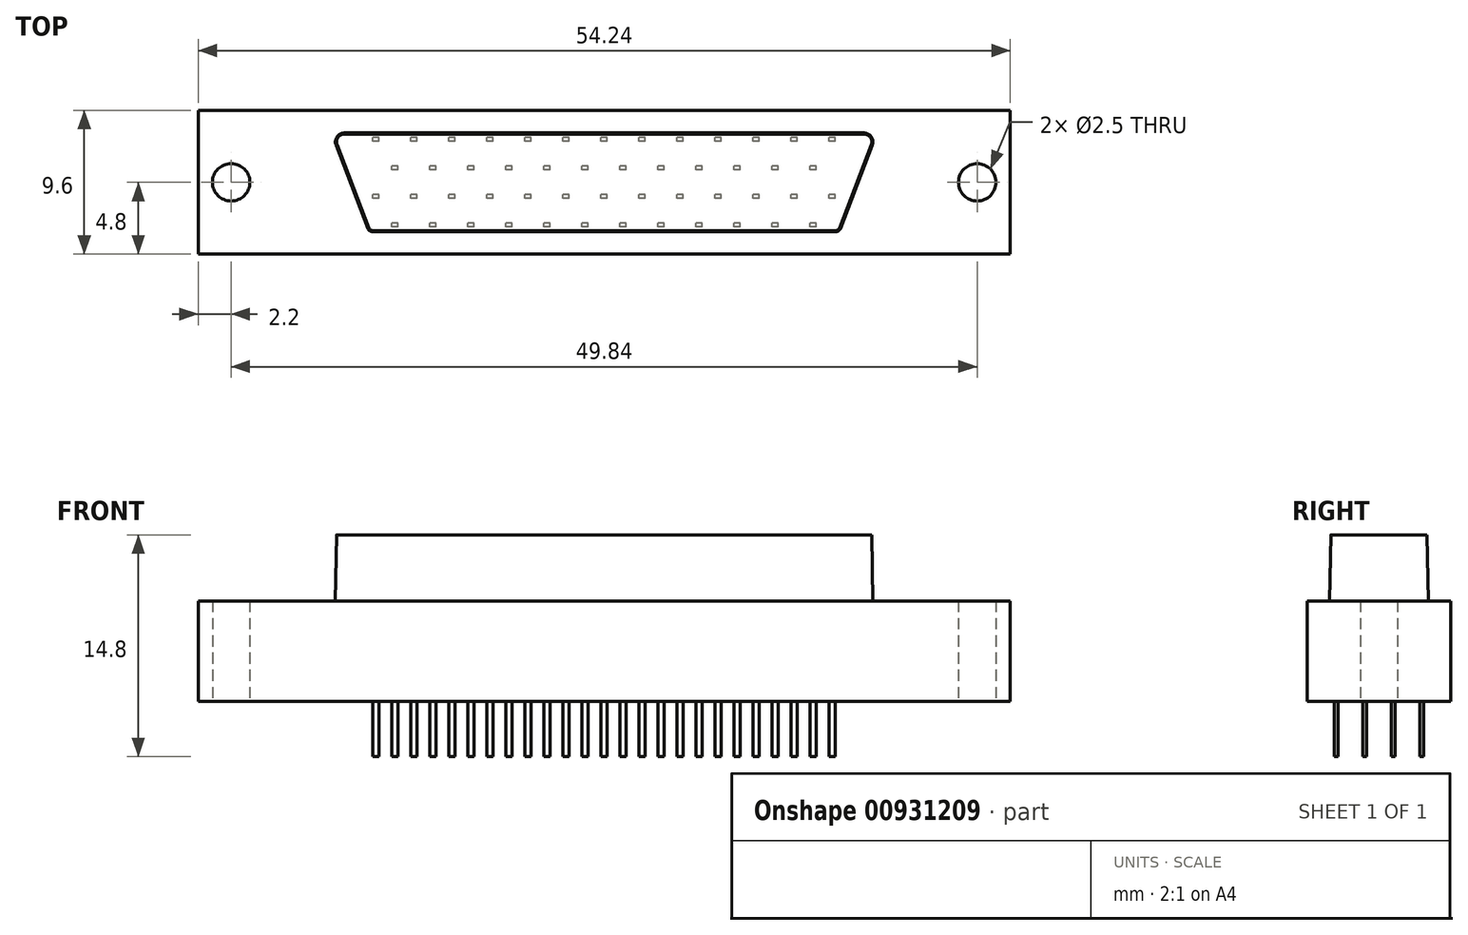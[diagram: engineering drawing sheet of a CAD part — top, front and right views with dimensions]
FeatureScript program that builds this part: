
annotation { "Feature Type Name" : "Feature", "Feature Type Description" : "" }
export const myFeature = defineFeature(function(context is Context, id is Id, definition is map)
    precondition{}
    {
        {
            var Q0;
            Q0=qCreatedBy(makeId("Top.planeOp"),FACE);
            var sketch = newSketch(context, id + "F0", { "sketchPlane" : qUnion([Q0])});
            skLineSegment(sketch, "E0.bottom", {"start": v(27.12, -4.8) * mm, "end": v(-27.12, -4.8) * mm});
            skLineSegment(sketch, "E0.top", {"start": v(27.12, 4.8) * mm, "end": v(-27.12, 4.8) * mm});
            skLineSegment(sketch, "E0.left", {"start": v(27.12, -4.8) * mm, "end": v(27.12, 4.8) * mm});
            skLineSegment(sketch, "E0.right", {"start": v(-27.12, -4.8) * mm, "end": v(-27.12, 4.8) * mm});
            skPoint(sketch, "E0.middle", {"position": v(0, 0) * mm});
            skCircle(sketch, "E1", {"center": v(24.92, 0) * mm, "radius": 1.25 * mm});
            skCircle(sketch, "E2.MirrorC", {"center": v(-24.92, 0) * mm, "radius": 1.25 * mm});
            skSolve(sketch);
        }
        {
            var Q0;
            Q0 = qSketchRegion(id + "F0", true);
            extrude(context, id + "F1", {"entities" : qUnion([Q0]), "depth" : 6.7 * mm, "offsetDistance" : 25 * mm, "symmetric" : true});
        }
        {
            var Q0;
            Q0=makeQuery(id+"F1.opExtrude","CAP_FACE",FACE,{"disambiguationData":[OSD([sQuery(id+"F0.wireOp",EDGE,"E0.bottom"),sQuery(id+"F0.wireOp",EDGE,"E0.top"),sQuery(id+"F0.wireOp",EDGE,"E0.left"),sQuery(id+"F0.wireOp",EDGE,"E0.right")])],"isStart":false});
            var sketch = newSketch(context, id + "F2", { "sketchPlane" : qUnion([Q0])});
            skLineSegment(sketch, "E3", {"start": v(-17.36, 3.3) * mm, "end": v(17.35, 3.3) * mm});
            skLineSegment(sketch, "E4", {"start": v(17.92, 2.48) * mm, "end": v(15.78, -3.1) * mm});
            skLineSegment(sketch, "E5", {"start": v(15.5, -3.3) * mm, "end": v(-15.5, -3.3) * mm});
            skLineSegment(sketch, "E6", {"start": v(-15.78, -3.1) * mm, "end": v(-17.92, 2.48) * mm});
            skPoint(sketch, "E7.visualSharp", {"position": v(-18.23, 3.3) * mm});
            skArc(sketch, "E7.filletArc", {"start": v(-17.36, 3.3) * mm, "mid": v(-17.85, 3.03) * mm, "end": v(-17.92, 2.48) * mm});
            skPoint(sketch, "E8.visualSharp", {"position": v(-15.7, -3.3) * mm});
            skArc(sketch, "E8.filletArc", {"start": v(-15.78, -3.1) * mm, "mid": v(-15.67, -3.24) * mm, "end": v(-15.5, -3.3) * mm});
            skPoint(sketch, "E9.visualSharp", {"position": v(18.23, 3.3) * mm});
            skArc(sketch, "E9.filletArc", {"start": v(17.92, 2.48) * mm, "mid": v(17.85, 3.03) * mm, "end": v(17.35, 3.3) * mm});
            skPoint(sketch, "E10.visualSharp", {"position": v(15.7, -3.3) * mm});
            skArc(sketch, "E10.filletArc", {"start": v(15.5, -3.3) * mm, "mid": v(15.67, -3.24) * mm, "end": v(15.78, -3.1) * mm});
            skSolve(sketch);
        }
        {
            var Q0;
            Q0=makeQuery(id+"F2.imprint","IMPRINT",FACE,{"disambiguationData":[TD([[makeQuery(id+"F2.imprint","IMPRINT",EDGE,{"derivedFrom":sQuery(id+"F2.wireOp",EDGE,"E3")}),-1.0]])]});
            extrude(context, id + "F3", {"entities" : qUnion([Q0]), "operationType" : NewBodyOperationType.ADD, "depth" : 4.4 * mm, "offsetDistance" : 25 * mm, "hasDraft" : true, "draftAngle" : 1 * degree, "draftPullDirection" : true});
        }
        {
            var Q0;
            Q0=makeQuery(id+"F1.opExtrude","CAP_FACE",FACE,{"disambiguationData":[OSD([sQuery(id+"F0.wireOp",EDGE,"E0.bottom"),sQuery(id+"F0.wireOp",EDGE,"E0.top"),sQuery(id+"F0.wireOp",EDGE,"E0.left"),sQuery(id+"F0.wireOp",EDGE,"E0.right"),sQuery(id+"F0.wireOp",EDGE,"E1"),sQuery(id+"F0.wireOp",EDGE,"E2.MirrorC")])],"isStart":true});
            var sketch = newSketch(context, id + "F4", { "sketchPlane" : qUnion([Q0])});
            skLineSegment(sketch, "E11.bottom", {"start": v(-15.03, -2.73) * mm, "end": v(-15.45, -2.73) * mm});
            skLineSegment(sketch, "E11.top", {"start": v(-15.03, -2.98) * mm, "end": v(-15.45, -2.98) * mm});
            skLineSegment(sketch, "E11.left", {"start": v(-15.03, -2.73) * mm, "end": v(-15.03, -2.98) * mm});
            skLineSegment(sketch, "E11.right", {"start": v(-15.45, -2.73) * mm, "end": v(-15.45, -2.98) * mm});
            skPoint(sketch, "E11.middle", {"position": v(-15.24, -2.86) * mm});
            skLineSegment(sketch, "E12.1.0.0", {"start": v(-12.49, -2.98) * mm, "end": v(-12.9, -2.98) * mm});
            skLineSegment(sketch, "E12.1.0.1", {"start": v(-12.9, -2.73) * mm, "end": v(-12.9, -2.98) * mm});
            skLineSegment(sketch, "E12.1.0.2", {"start": v(-12.49, -2.73) * mm, "end": v(-12.9, -2.73) * mm});
            skLineSegment(sketch, "E12.1.0.3", {"start": v(-12.49, -2.73) * mm, "end": v(-12.49, -2.98) * mm});
            skPoint(sketch, "E12.1.0.4", {"position": v(-12.7, -2.86) * mm});
            skLineSegment(sketch, "E12.2.0.0", {"start": v(-9.95, -2.98) * mm, "end": v(-10.37, -2.98) * mm});
            skLineSegment(sketch, "E12.2.0.1", {"start": v(-10.37, -2.73) * mm, "end": v(-10.37, -2.98) * mm});
            skLineSegment(sketch, "E12.2.0.2", {"start": v(-9.95, -2.73) * mm, "end": v(-10.37, -2.73) * mm});
            skLineSegment(sketch, "E12.2.0.3", {"start": v(-9.95, -2.73) * mm, "end": v(-9.95, -2.98) * mm});
            skPoint(sketch, "E12.2.0.4", {"position": v(-10.16, -2.86) * mm});
            skLineSegment(sketch, "E12.3.0.0", {"start": v(-7.4, -2.98) * mm, "end": v(-7.83, -2.98) * mm});
            skLineSegment(sketch, "E12.3.0.1", {"start": v(-7.83, -2.73) * mm, "end": v(-7.83, -2.98) * mm});
            skLineSegment(sketch, "E12.3.0.2", {"start": v(-7.4, -2.73) * mm, "end": v(-7.83, -2.73) * mm});
            skLineSegment(sketch, "E12.3.0.3", {"start": v(-7.4, -2.73) * mm, "end": v(-7.4, -2.98) * mm});
            skPoint(sketch, "E12.3.0.4", {"position": v(-7.62, -2.86) * mm});
            skLineSegment(sketch, "E12.4.0.0", {"start": v(-4.87, -2.98) * mm, "end": v(-5.29, -2.98) * mm});
            skLineSegment(sketch, "E12.4.0.1", {"start": v(-5.29, -2.73) * mm, "end": v(-5.29, -2.98) * mm});
            skLineSegment(sketch, "E12.4.0.2", {"start": v(-4.87, -2.73) * mm, "end": v(-5.29, -2.73) * mm});
            skLineSegment(sketch, "E12.4.0.3", {"start": v(-4.87, -2.73) * mm, "end": v(-4.87, -2.98) * mm});
            skPoint(sketch, "E12.4.0.4", {"position": v(-5.08, -2.86) * mm});
            skLineSegment(sketch, "E12.5.0.0", {"start": v(-2.33, -2.98) * mm, "end": v(-2.75, -2.98) * mm});
            skLineSegment(sketch, "E12.5.0.1", {"start": v(-2.75, -2.73) * mm, "end": v(-2.75, -2.98) * mm});
            skLineSegment(sketch, "E12.5.0.2", {"start": v(-2.33, -2.73) * mm, "end": v(-2.75, -2.73) * mm});
            skLineSegment(sketch, "E12.5.0.3", {"start": v(-2.33, -2.73) * mm, "end": v(-2.33, -2.98) * mm});
            skPoint(sketch, "E12.5.0.4", {"position": v(-2.54, -2.86) * mm});
            skLineSegment(sketch, "E12.6.0.0", {"start": v(0.2, -2.98) * mm, "end": v(-0.2, -2.98) * mm});
            skLineSegment(sketch, "E12.6.0.1", {"start": v(-0.2, -2.73) * mm, "end": v(-0.2, -2.98) * mm});
            skLineSegment(sketch, "E12.6.0.2", {"start": v(0.2, -2.73) * mm, "end": v(-0.2, -2.73) * mm});
            skLineSegment(sketch, "E12.6.0.3", {"start": v(0.2, -2.73) * mm, "end": v(0.2, -2.98) * mm});
            skPoint(sketch, "E12.6.0.4", {"position": v(0, -2.86) * mm});
            skLineSegment(sketch, "E12.7.0.0", {"start": v(2.75, -2.98) * mm, "end": v(2.33, -2.98) * mm});
            skLineSegment(sketch, "E12.7.0.1", {"start": v(2.33, -2.73) * mm, "end": v(2.33, -2.98) * mm});
            skLineSegment(sketch, "E12.7.0.2", {"start": v(2.75, -2.73) * mm, "end": v(2.33, -2.73) * mm});
            skLineSegment(sketch, "E12.7.0.3", {"start": v(2.75, -2.73) * mm, "end": v(2.75, -2.98) * mm});
            skPoint(sketch, "E12.7.0.4", {"position": v(2.54, -2.86) * mm});
            skLineSegment(sketch, "E12.8.0.0", {"start": v(5.29, -2.98) * mm, "end": v(4.87, -2.98) * mm});
            skLineSegment(sketch, "E12.8.0.1", {"start": v(4.87, -2.73) * mm, "end": v(4.87, -2.98) * mm});
            skLineSegment(sketch, "E12.8.0.2", {"start": v(5.29, -2.73) * mm, "end": v(4.87, -2.73) * mm});
            skLineSegment(sketch, "E12.8.0.3", {"start": v(5.29, -2.73) * mm, "end": v(5.29, -2.98) * mm});
            skPoint(sketch, "E12.8.0.4", {"position": v(5.08, -2.86) * mm});
            skLineSegment(sketch, "E12.9.0.0", {"start": v(7.83, -2.98) * mm, "end": v(7.4, -2.98) * mm});
            skLineSegment(sketch, "E12.9.0.1", {"start": v(7.4, -2.73) * mm, "end": v(7.4, -2.98) * mm});
            skLineSegment(sketch, "E12.9.0.2", {"start": v(7.83, -2.73) * mm, "end": v(7.4, -2.73) * mm});
            skLineSegment(sketch, "E12.9.0.3", {"start": v(7.83, -2.73) * mm, "end": v(7.83, -2.98) * mm});
            skPoint(sketch, "E12.9.0.4", {"position": v(7.62, -2.86) * mm});
            skLineSegment(sketch, "E12.10.0.0", {"start": v(10.37, -2.98) * mm, "end": v(9.95, -2.98) * mm});
            skLineSegment(sketch, "E12.10.0.1", {"start": v(9.95, -2.73) * mm, "end": v(9.95, -2.98) * mm});
            skLineSegment(sketch, "E12.10.0.2", {"start": v(10.37, -2.73) * mm, "end": v(9.95, -2.73) * mm});
            skLineSegment(sketch, "E12.10.0.3", {"start": v(10.37, -2.73) * mm, "end": v(10.37, -2.98) * mm});
            skPoint(sketch, "E12.10.0.4", {"position": v(10.16, -2.86) * mm});
            skLineSegment(sketch, "E12.11.0.0", {"start": v(12.9, -2.98) * mm, "end": v(12.5, -2.98) * mm});
            skLineSegment(sketch, "E12.11.0.1", {"start": v(12.49, -2.73) * mm, "end": v(12.49, -2.98) * mm});
            skLineSegment(sketch, "E12.11.0.2", {"start": v(12.9, -2.73) * mm, "end": v(12.5, -2.73) * mm});
            skLineSegment(sketch, "E12.11.0.3", {"start": v(12.9, -2.73) * mm, "end": v(12.9, -2.98) * mm});
            skPoint(sketch, "E12.11.0.4", {"position": v(12.7, -2.86) * mm});
            skLineSegment(sketch, "E12.12.0.0", {"start": v(15.45, -2.98) * mm, "end": v(15.03, -2.98) * mm});
            skLineSegment(sketch, "E12.12.0.1", {"start": v(15.03, -2.73) * mm, "end": v(15.03, -2.98) * mm});
            skLineSegment(sketch, "E12.12.0.2", {"start": v(15.45, -2.73) * mm, "end": v(15.03, -2.73) * mm});
            skLineSegment(sketch, "E12.12.0.3", {"start": v(15.45, -2.73) * mm, "end": v(15.45, -2.98) * mm});
            skPoint(sketch, "E12.12.0.4", {"position": v(15.24, -2.86) * mm});
            skLineSegment(sketch, "E12.direction1", {"start": v(-15.45, -2.98) * mm, "end": v(-12.9, -2.98) * mm, "construction": true});
            skLineSegment(sketch, "E13.bottom", {"start": v(-13.76, -0.83) * mm, "end": v(-14.18, -0.83) * mm});
            skLineSegment(sketch, "E13.top", {"start": v(-13.76, -1.08) * mm, "end": v(-14.18, -1.08) * mm});
            skLineSegment(sketch, "E13.left", {"start": v(-13.76, -0.83) * mm, "end": v(-13.76, -1.08) * mm});
            skLineSegment(sketch, "E13.right", {"start": v(-14.18, -0.83) * mm, "end": v(-14.18, -1.08) * mm});
            skPoint(sketch, "E13.middle", {"position": v(-13.97, -0.95) * mm});
            skLineSegment(sketch, "E14.direction1", {"start": v(-14.18, -1.08) * mm, "end": v(-11.64, -1.08) * mm, "construction": true});
            skLineSegment(sketch, "E15.1.0.0", {"start": v(-11.22, -0.83) * mm, "end": v(-11.22, -1.08) * mm});
            skLineSegment(sketch, "E15.1.0.1", {"start": v(-11.22, -1.08) * mm, "end": v(-11.64, -1.08) * mm});
            skLineSegment(sketch, "E15.1.0.2", {"start": v(-11.64, -0.83) * mm, "end": v(-11.64, -1.08) * mm});
            skLineSegment(sketch, "E15.1.0.3", {"start": v(-11.22, -0.83) * mm, "end": v(-11.64, -0.83) * mm});
            skPoint(sketch, "E15.1.0.4", {"position": v(-11.43, -0.95) * mm});
            skLineSegment(sketch, "E15.2.0.0", {"start": v(-8.68, -0.83) * mm, "end": v(-8.68, -1.08) * mm});
            skLineSegment(sketch, "E15.2.0.1", {"start": v(-8.68, -1.08) * mm, "end": v(-9.1, -1.08) * mm});
            skLineSegment(sketch, "E15.2.0.2", {"start": v(-9.1, -0.83) * mm, "end": v(-9.1, -1.08) * mm});
            skLineSegment(sketch, "E15.2.0.3", {"start": v(-8.68, -0.83) * mm, "end": v(-9.1, -0.83) * mm});
            skPoint(sketch, "E15.2.0.4", {"position": v(-8.89, -0.95) * mm});
            skLineSegment(sketch, "E15.3.0.0", {"start": v(-6.14, -0.83) * mm, "end": v(-6.14, -1.08) * mm});
            skLineSegment(sketch, "E15.3.0.1", {"start": v(-6.14, -1.08) * mm, "end": v(-6.56, -1.08) * mm});
            skLineSegment(sketch, "E15.3.0.2", {"start": v(-6.56, -0.83) * mm, "end": v(-6.56, -1.08) * mm});
            skLineSegment(sketch, "E15.3.0.3", {"start": v(-6.14, -0.83) * mm, "end": v(-6.56, -0.83) * mm});
            skPoint(sketch, "E15.3.0.4", {"position": v(-6.35, -0.95) * mm});
            skLineSegment(sketch, "E15.4.0.0", {"start": v(-3.6, -0.83) * mm, "end": v(-3.6, -1.08) * mm});
            skLineSegment(sketch, "E15.4.0.1", {"start": v(-3.6, -1.08) * mm, "end": v(-4.02, -1.08) * mm});
            skLineSegment(sketch, "E15.4.0.2", {"start": v(-4.02, -0.83) * mm, "end": v(-4.02, -1.08) * mm});
            skLineSegment(sketch, "E15.4.0.3", {"start": v(-3.6, -0.83) * mm, "end": v(-4.02, -0.83) * mm});
            skPoint(sketch, "E15.4.0.4", {"position": v(-3.8, -0.95) * mm});
            skLineSegment(sketch, "E15.5.0.0", {"start": v(-1.06, -0.83) * mm, "end": v(-1.06, -1.08) * mm});
            skLineSegment(sketch, "E15.5.0.1", {"start": v(-1.06, -1.08) * mm, "end": v(-1.48, -1.08) * mm});
            skLineSegment(sketch, "E15.5.0.2", {"start": v(-1.48, -0.83) * mm, "end": v(-1.48, -1.08) * mm});
            skLineSegment(sketch, "E15.5.0.3", {"start": v(-1.06, -0.83) * mm, "end": v(-1.48, -0.83) * mm});
            skPoint(sketch, "E15.5.0.4", {"position": v(-1.27, -0.95) * mm});
            skLineSegment(sketch, "E15.6.0.0", {"start": v(1.48, -0.83) * mm, "end": v(1.48, -1.08) * mm});
            skLineSegment(sketch, "E15.6.0.1", {"start": v(1.48, -1.08) * mm, "end": v(1.06, -1.08) * mm});
            skLineSegment(sketch, "E15.6.0.2", {"start": v(1.06, -0.83) * mm, "end": v(1.06, -1.08) * mm});
            skLineSegment(sketch, "E15.6.0.3", {"start": v(1.48, -0.83) * mm, "end": v(1.06, -0.83) * mm});
            skPoint(sketch, "E15.6.0.4", {"position": v(1.27, -0.95) * mm});
            skLineSegment(sketch, "E15.7.0.0", {"start": v(4.02, -0.83) * mm, "end": v(4.02, -1.08) * mm});
            skLineSegment(sketch, "E15.7.0.1", {"start": v(4.02, -1.08) * mm, "end": v(3.6, -1.08) * mm});
            skLineSegment(sketch, "E15.7.0.2", {"start": v(3.6, -0.83) * mm, "end": v(3.6, -1.08) * mm});
            skLineSegment(sketch, "E15.7.0.3", {"start": v(4.02, -0.83) * mm, "end": v(3.6, -0.83) * mm});
            skPoint(sketch, "E15.7.0.4", {"position": v(3.81, -0.95) * mm});
            skLineSegment(sketch, "E15.8.0.0", {"start": v(6.56, -0.83) * mm, "end": v(6.56, -1.08) * mm});
            skLineSegment(sketch, "E15.8.0.1", {"start": v(6.56, -1.08) * mm, "end": v(6.14, -1.08) * mm});
            skLineSegment(sketch, "E15.8.0.2", {"start": v(6.14, -0.83) * mm, "end": v(6.14, -1.08) * mm});
            skLineSegment(sketch, "E15.8.0.3", {"start": v(6.56, -0.83) * mm, "end": v(6.14, -0.83) * mm});
            skPoint(sketch, "E15.8.0.4", {"position": v(6.35, -0.95) * mm});
            skLineSegment(sketch, "E15.9.0.0", {"start": v(9.1, -0.83) * mm, "end": v(9.1, -1.08) * mm});
            skLineSegment(sketch, "E15.9.0.1", {"start": v(9.1, -1.08) * mm, "end": v(8.68, -1.08) * mm});
            skLineSegment(sketch, "E15.9.0.2", {"start": v(8.68, -0.83) * mm, "end": v(8.68, -1.08) * mm});
            skLineSegment(sketch, "E15.9.0.3", {"start": v(9.1, -0.83) * mm, "end": v(8.68, -0.83) * mm});
            skPoint(sketch, "E15.9.0.4", {"position": v(8.9, -0.95) * mm});
            skLineSegment(sketch, "E15.10.0.0", {"start": v(11.64, -0.83) * mm, "end": v(11.64, -1.08) * mm});
            skLineSegment(sketch, "E15.10.0.1", {"start": v(11.64, -1.08) * mm, "end": v(11.22, -1.08) * mm});
            skLineSegment(sketch, "E15.10.0.2", {"start": v(11.22, -0.83) * mm, "end": v(11.22, -1.08) * mm});
            skLineSegment(sketch, "E15.10.0.3", {"start": v(11.64, -0.83) * mm, "end": v(11.22, -0.83) * mm});
            skPoint(sketch, "E15.10.0.4", {"position": v(11.43, -0.95) * mm});
            skLineSegment(sketch, "E15.11.0.0", {"start": v(14.18, -0.83) * mm, "end": v(14.18, -1.08) * mm});
            skLineSegment(sketch, "E15.11.0.1", {"start": v(14.18, -1.08) * mm, "end": v(13.76, -1.08) * mm});
            skLineSegment(sketch, "E15.11.0.2", {"start": v(13.76, -0.83) * mm, "end": v(13.76, -1.08) * mm});
            skLineSegment(sketch, "E15.11.0.3", {"start": v(14.18, -0.83) * mm, "end": v(13.76, -0.83) * mm});
            skPoint(sketch, "E15.11.0.4", {"position": v(13.97, -0.95) * mm});
            skPoint(sketch, "E16.1.0.0", {"position": v(2.54, 0.95) * mm});
            skPoint(sketch, "E16.1.0.1", {"position": v(-10.16, 0.95) * mm});
            skPoint(sketch, "E16.1.0.2", {"position": v(-7.62, 0.95) * mm});
            skPoint(sketch, "E16.1.0.3", {"position": v(0, 0.95) * mm});
            skPoint(sketch, "E16.1.0.4", {"position": v(-5.08, 0.95) * mm});
            skPoint(sketch, "E16.1.0.5", {"position": v(10.16, 0.95) * mm});
            skPoint(sketch, "E16.1.0.6", {"position": v(11.43, 2.86) * mm});
            skPoint(sketch, "E16.1.0.7", {"position": v(15.24, 0.95) * mm});
            skPoint(sketch, "E16.1.0.8", {"position": v(3.81, 2.86) * mm});
            skPoint(sketch, "E16.1.0.9", {"position": v(6.35, 2.86) * mm});
            skPoint(sketch, "E16.1.0.10", {"position": v(-15.24, 0.95) * mm});
            skPoint(sketch, "E16.1.0.11", {"position": v(13.97, 2.86) * mm});
            skPoint(sketch, "E16.1.0.12", {"position": v(5.08, 0.95) * mm});
            skPoint(sketch, "E16.1.0.13", {"position": v(1.27, 2.86) * mm});
            skPoint(sketch, "E16.1.0.14", {"position": v(-3.8, 2.86) * mm});
            skPoint(sketch, "E16.1.0.15", {"position": v(-2.54, 0.95) * mm});
            skPoint(sketch, "E16.1.0.16", {"position": v(-1.27, 2.86) * mm});
            skPoint(sketch, "E16.1.0.17", {"position": v(12.7, 0.95) * mm});
            skPoint(sketch, "E16.1.0.18", {"position": v(-6.35, 2.86) * mm});
            skPoint(sketch, "E16.1.0.19", {"position": v(-13.97, 2.86) * mm});
            skPoint(sketch, "E16.1.0.20", {"position": v(8.9, 2.86) * mm});
            skPoint(sketch, "E16.1.0.21", {"position": v(-11.43, 2.86) * mm});
            skPoint(sketch, "E16.1.0.22", {"position": v(7.62, 0.95) * mm});
            skPoint(sketch, "E16.1.0.23", {"position": v(-8.89, 2.86) * mm});
            skLineSegment(sketch, "E16.1.0.24", {"start": v(-14.18, 2.73) * mm, "end": v(-11.64, 2.73) * mm, "construction": true});
            skPoint(sketch, "E16.1.0.25", {"position": v(-12.7, 0.95) * mm});
            skLineSegment(sketch, "E16.1.0.26", {"start": v(-15.45, 0.83) * mm, "end": v(-12.9, 0.83) * mm, "construction": true});
            skLineSegment(sketch, "E16.1.0.27", {"start": v(-14.18, 2.73) * mm, "end": v(-11.64, 2.73) * mm, "construction": true});
            skLineSegment(sketch, "E16.1.0.28", {"start": v(9.1, 2.73) * mm, "end": v(8.68, 2.73) * mm});
            skLineSegment(sketch, "E16.1.0.29", {"start": v(1.06, 2.98) * mm, "end": v(1.06, 2.73) * mm});
            skLineSegment(sketch, "E16.1.0.30", {"start": v(9.1, 2.98) * mm, "end": v(8.68, 2.98) * mm});
            skLineSegment(sketch, "E16.1.0.31", {"start": v(15.45, 1.08) * mm, "end": v(15.03, 1.08) * mm});
            skLineSegment(sketch, "E16.1.0.32", {"start": v(11.64, 2.98) * mm, "end": v(11.22, 2.98) * mm});
            skLineSegment(sketch, "E16.1.0.33", {"start": v(-3.6, 2.73) * mm, "end": v(-4.02, 2.73) * mm});
            skLineSegment(sketch, "E16.1.0.34", {"start": v(-2.33, 0.83) * mm, "end": v(-2.75, 0.83) * mm});
            skLineSegment(sketch, "E16.1.0.35", {"start": v(11.64, 2.73) * mm, "end": v(11.22, 2.73) * mm});
            skLineSegment(sketch, "E16.1.0.36", {"start": v(10.37, 1.08) * mm, "end": v(9.95, 1.08) * mm});
            skLineSegment(sketch, "E16.1.0.37", {"start": v(2.33, 1.08) * mm, "end": v(2.33, 0.83) * mm});
            skLineSegment(sketch, "E16.1.0.38", {"start": v(12.9, 1.08) * mm, "end": v(12.5, 1.08) * mm});
            skLineSegment(sketch, "E16.1.0.39", {"start": v(14.18, 2.98) * mm, "end": v(14.18, 2.73) * mm});
            skLineSegment(sketch, "E16.1.0.40", {"start": v(13.76, 2.98) * mm, "end": v(13.76, 2.73) * mm});
            skLineSegment(sketch, "E16.1.0.41", {"start": v(-2.33, 1.08) * mm, "end": v(-2.33, 0.83) * mm});
            skLineSegment(sketch, "E16.1.0.42", {"start": v(0.2, 0.83) * mm, "end": v(-0.2, 0.83) * mm});
            skLineSegment(sketch, "E16.1.0.43", {"start": v(10.37, 1.08) * mm, "end": v(10.37, 0.83) * mm});
            skLineSegment(sketch, "E16.1.0.44", {"start": v(2.75, 1.08) * mm, "end": v(2.75, 0.83) * mm});
            skLineSegment(sketch, "E16.1.0.45", {"start": v(-1.06, 2.73) * mm, "end": v(-1.48, 2.73) * mm});
            skLineSegment(sketch, "E16.1.0.46", {"start": v(7.4, 1.08) * mm, "end": v(7.4, 0.83) * mm});
            skLineSegment(sketch, "E16.1.0.47", {"start": v(-8.68, 2.98) * mm, "end": v(-8.68, 2.73) * mm});
            skLineSegment(sketch, "E16.1.0.48", {"start": v(-7.4, 1.08) * mm, "end": v(-7.83, 1.08) * mm});
            skLineSegment(sketch, "E16.1.0.49", {"start": v(1.48, 2.73) * mm, "end": v(1.06, 2.73) * mm});
            skLineSegment(sketch, "E16.1.0.50", {"start": v(0.2, 1.08) * mm, "end": v(-0.2, 1.08) * mm});
            skLineSegment(sketch, "E16.1.0.51", {"start": v(4.87, 1.08) * mm, "end": v(4.87, 0.83) * mm});
            skLineSegment(sketch, "E16.1.0.52", {"start": v(-4.87, 1.08) * mm, "end": v(-4.87, 0.83) * mm});
            skLineSegment(sketch, "E16.1.0.53", {"start": v(-8.68, 2.73) * mm, "end": v(-9.1, 2.73) * mm});
            skLineSegment(sketch, "E16.1.0.54", {"start": v(-7.4, 1.08) * mm, "end": v(-7.4, 0.83) * mm});
            skLineSegment(sketch, "E16.1.0.55", {"start": v(5.29, 1.08) * mm, "end": v(4.87, 1.08) * mm});
            skLineSegment(sketch, "E16.1.0.56", {"start": v(7.83, 0.83) * mm, "end": v(7.4, 0.83) * mm});
            skLineSegment(sketch, "E16.1.0.57", {"start": v(2.75, 1.08) * mm, "end": v(2.33, 1.08) * mm});
            skLineSegment(sketch, "E16.1.0.58", {"start": v(12.9, 1.08) * mm, "end": v(12.9, 0.83) * mm});
            skLineSegment(sketch, "E16.1.0.59", {"start": v(1.48, 2.98) * mm, "end": v(1.48, 2.73) * mm});
            skLineSegment(sketch, "E16.1.0.60", {"start": v(14.18, 2.98) * mm, "end": v(13.76, 2.98) * mm});
            skLineSegment(sketch, "E16.1.0.61", {"start": v(6.56, 2.73) * mm, "end": v(6.14, 2.73) * mm});
            skLineSegment(sketch, "E16.1.0.62", {"start": v(4.02, 2.98) * mm, "end": v(3.6, 2.98) * mm});
            skLineSegment(sketch, "E16.1.0.63", {"start": v(-6.14, 2.73) * mm, "end": v(-6.56, 2.73) * mm});
            skLineSegment(sketch, "E16.1.0.64", {"start": v(3.6, 2.98) * mm, "end": v(3.6, 2.73) * mm});
            skLineSegment(sketch, "E16.1.0.65", {"start": v(10.37, 0.83) * mm, "end": v(9.95, 0.83) * mm});
            skLineSegment(sketch, "E16.1.0.66", {"start": v(-2.75, 1.08) * mm, "end": v(-2.75, 0.83) * mm});
            skLineSegment(sketch, "E16.1.0.67", {"start": v(7.83, 1.08) * mm, "end": v(7.83, 0.83) * mm});
            skLineSegment(sketch, "E16.1.0.68", {"start": v(-7.83, 1.08) * mm, "end": v(-7.83, 0.83) * mm});
            skLineSegment(sketch, "E16.1.0.69", {"start": v(14.18, 2.73) * mm, "end": v(13.76, 2.73) * mm});
            skLineSegment(sketch, "E16.1.0.70", {"start": v(-1.48, 2.98) * mm, "end": v(-1.48, 2.73) * mm});
            skLineSegment(sketch, "E16.1.0.71", {"start": v(-6.14, 2.98) * mm, "end": v(-6.14, 2.73) * mm});
            skLineSegment(sketch, "E16.1.0.72", {"start": v(8.68, 2.98) * mm, "end": v(8.68, 2.73) * mm});
            skLineSegment(sketch, "E16.1.0.73", {"start": v(9.1, 2.98) * mm, "end": v(9.1, 2.73) * mm});
            skLineSegment(sketch, "E16.1.0.74", {"start": v(4.02, 2.73) * mm, "end": v(3.6, 2.73) * mm});
            skLineSegment(sketch, "E16.1.0.75", {"start": v(5.29, 1.08) * mm, "end": v(5.29, 0.83) * mm});
            skLineSegment(sketch, "E16.1.0.76", {"start": v(-5.29, 1.08) * mm, "end": v(-5.29, 0.83) * mm});
            skLineSegment(sketch, "E16.1.0.77", {"start": v(1.48, 2.98) * mm, "end": v(1.06, 2.98) * mm});
            skLineSegment(sketch, "E16.1.0.78", {"start": v(-4.87, 1.08) * mm, "end": v(-5.29, 1.08) * mm});
            skLineSegment(sketch, "E16.1.0.79", {"start": v(11.64, 2.98) * mm, "end": v(11.64, 2.73) * mm});
            skLineSegment(sketch, "E16.1.0.80", {"start": v(12.9, 0.83) * mm, "end": v(12.5, 0.83) * mm});
            skLineSegment(sketch, "E16.1.0.81", {"start": v(-4.02, 2.98) * mm, "end": v(-4.02, 2.73) * mm});
            skLineSegment(sketch, "E16.1.0.82", {"start": v(-8.68, 2.98) * mm, "end": v(-9.1, 2.98) * mm});
            skLineSegment(sketch, "E16.1.0.83", {"start": v(2.75, 0.83) * mm, "end": v(2.33, 0.83) * mm});
            skLineSegment(sketch, "E16.1.0.84", {"start": v(4.02, 2.98) * mm, "end": v(4.02, 2.73) * mm});
            skLineSegment(sketch, "E16.1.0.85", {"start": v(6.14, 2.98) * mm, "end": v(6.14, 2.73) * mm});
            skLineSegment(sketch, "E16.1.0.86", {"start": v(-3.6, 2.98) * mm, "end": v(-4.02, 2.98) * mm});
            skLineSegment(sketch, "E16.1.0.87", {"start": v(9.95, 1.08) * mm, "end": v(9.95, 0.83) * mm});
            skLineSegment(sketch, "E16.1.0.88", {"start": v(15.45, 1.08) * mm, "end": v(15.45, 0.83) * mm});
            skLineSegment(sketch, "E16.1.0.89", {"start": v(6.56, 2.98) * mm, "end": v(6.14, 2.98) * mm});
            skLineSegment(sketch, "E16.1.0.90", {"start": v(-0.2, 1.08) * mm, "end": v(-0.2, 0.83) * mm});
            skLineSegment(sketch, "E16.1.0.91", {"start": v(15.03, 1.08) * mm, "end": v(15.03, 0.83) * mm});
            skLineSegment(sketch, "E16.1.0.92", {"start": v(-1.06, 2.98) * mm, "end": v(-1.06, 2.73) * mm});
            skLineSegment(sketch, "E16.1.0.93", {"start": v(-1.06, 2.98) * mm, "end": v(-1.48, 2.98) * mm});
            skLineSegment(sketch, "E16.1.0.94", {"start": v(-6.14, 2.98) * mm, "end": v(-6.56, 2.98) * mm});
            skLineSegment(sketch, "E16.1.0.95", {"start": v(-4.87, 0.83) * mm, "end": v(-5.29, 0.83) * mm});
            skLineSegment(sketch, "E16.1.0.96", {"start": v(5.29, 0.83) * mm, "end": v(4.87, 0.83) * mm});
            skLineSegment(sketch, "E16.1.0.97", {"start": v(15.45, 0.83) * mm, "end": v(15.03, 0.83) * mm});
            skLineSegment(sketch, "E16.1.0.98", {"start": v(-9.1, 2.98) * mm, "end": v(-9.1, 2.73) * mm});
            skLineSegment(sketch, "E16.1.0.99", {"start": v(-3.6, 2.98) * mm, "end": v(-3.6, 2.73) * mm});
            skLineSegment(sketch, "E16.1.0.100", {"start": v(6.56, 2.98) * mm, "end": v(6.56, 2.73) * mm});
            skLineSegment(sketch, "E16.1.0.101", {"start": v(-2.33, 1.08) * mm, "end": v(-2.75, 1.08) * mm});
            skLineSegment(sketch, "E16.1.0.102", {"start": v(7.83, 1.08) * mm, "end": v(7.4, 1.08) * mm});
            skLineSegment(sketch, "E16.1.0.103", {"start": v(-7.4, 0.83) * mm, "end": v(-7.83, 0.83) * mm});
            skLineSegment(sketch, "E16.1.0.104", {"start": v(-9.95, 1.08) * mm, "end": v(-9.95, 0.83) * mm});
            skLineSegment(sketch, "E16.1.0.105", {"start": v(-9.95, 1.08) * mm, "end": v(-10.37, 1.08) * mm});
            skLineSegment(sketch, "E16.1.0.106", {"start": v(-10.37, 1.08) * mm, "end": v(-10.37, 0.83) * mm});
            skLineSegment(sketch, "E16.1.0.107", {"start": v(-9.95, 0.83) * mm, "end": v(-10.37, 0.83) * mm});
            skLineSegment(sketch, "E16.1.0.108", {"start": v(-15.03, 0.83) * mm, "end": v(-15.45, 0.83) * mm});
            skLineSegment(sketch, "E16.1.0.109", {"start": v(-6.56, 2.98) * mm, "end": v(-6.56, 2.73) * mm});
            skLineSegment(sketch, "E16.1.0.110", {"start": v(11.22, 2.98) * mm, "end": v(11.22, 2.73) * mm});
            skLineSegment(sketch, "E16.1.0.111", {"start": v(-15.45, 1.08) * mm, "end": v(-15.45, 0.83) * mm});
            skLineSegment(sketch, "E16.1.0.112", {"start": v(-15.03, 1.08) * mm, "end": v(-15.03, 0.83) * mm});
            skLineSegment(sketch, "E16.1.0.113", {"start": v(-15.03, 1.08) * mm, "end": v(-15.45, 1.08) * mm});
            skLineSegment(sketch, "E16.1.0.114", {"start": v(12.49, 1.08) * mm, "end": v(12.49, 0.83) * mm});
            skLineSegment(sketch, "E16.1.0.115", {"start": v(0.2, 1.08) * mm, "end": v(0.2, 0.83) * mm});
            skLineSegment(sketch, "E16.1.0.116", {"start": v(-14.18, 2.98) * mm, "end": v(-14.18, 2.73) * mm});
            skLineSegment(sketch, "E16.1.0.117", {"start": v(-11.22, 2.98) * mm, "end": v(-11.22, 2.73) * mm});
            skLineSegment(sketch, "E16.1.0.118", {"start": v(-11.22, 2.98) * mm, "end": v(-11.64, 2.98) * mm});
            skLineSegment(sketch, "E16.1.0.119", {"start": v(-11.64, 2.98) * mm, "end": v(-11.64, 2.73) * mm});
            skLineSegment(sketch, "E16.1.0.120", {"start": v(-13.76, 2.98) * mm, "end": v(-13.76, 2.73) * mm});
            skLineSegment(sketch, "E16.1.0.121", {"start": v(-12.49, 0.83) * mm, "end": v(-12.9, 0.83) * mm});
            skLineSegment(sketch, "E16.1.0.122", {"start": v(-12.49, 1.08) * mm, "end": v(-12.49, 0.83) * mm});
            skLineSegment(sketch, "E16.1.0.123", {"start": v(-12.9, 1.08) * mm, "end": v(-12.9, 0.83) * mm});
            skLineSegment(sketch, "E16.1.0.124", {"start": v(-13.76, 2.98) * mm, "end": v(-14.18, 2.98) * mm});
            skLineSegment(sketch, "E16.1.0.125", {"start": v(-12.49, 1.08) * mm, "end": v(-12.9, 1.08) * mm});
            skLineSegment(sketch, "E16.1.0.126", {"start": v(-11.22, 2.73) * mm, "end": v(-11.64, 2.73) * mm});
            skLineSegment(sketch, "E16.1.0.127", {"start": v(-13.76, 2.73) * mm, "end": v(-14.18, 2.73) * mm});
            skLineSegment(sketch, "E16.direction1", {"start": v(-15.45, -2.98) * mm, "end": v(-15.45, 0.83) * mm, "construction": true});
            skSolve(sketch);
        }
        {
            var Q0;
            Q0 = qSketchRegion(id + "F4", true);
            extrude(context, id + "F5", {"entities" : qUnion([Q0]), "operationType" : NewBodyOperationType.ADD, "depth" : 3.7 * mm, "offsetDistance" : 25 * mm});
        }
    });
